# Revit family: 55152_PRESTO_Volta Mitigeur électronique sur plage pour lavabo_FR
name_source: partatom
category: Appareils sanitaires
revit_build: Autodesk Revit 2018 (Build: 20190510_1515(x64)
units: mm (PartAtom-declared; Revit-internal decimal feet)

## family parameters
Basée sur le plan de construction = Non
Cote de connecteur circulaire = Utiliser le diamètre
Couper avec des vides une fois chargée = Non
Partagée = Non
Point de calcul de pièce = Non
Toujours verticalement = Oui
Type d'élément = Normal

## types (1)
- 55152 Presto Volta Mitigeur électronique sur plage pour lavabo
    Adresse = 7, RUE RACINE - 92542 MONTROUGE CEDEX FRANCE
    Charge apparente = 0 VA
    Description = Robinet temporisé mitigeur électronique sur plage pour lavabo
    Diamètre arrivée d'eau = 12 mm  [stored 0.0393701 ft]
    Débit = 8 l/mn par limiteur de débit intégré
    Fabricant = LES ROBINETSPRESTO S.A.
    Facteur de puissance = 1
    Famille produit = Lavabo
    Flux arrivée d'eau = 0.0 L/s
    Garantie = 10
    Groupe produit = -
    Hauteur = 157 mm  [stored 0.515092 ft]
    Longueur = 71 mm
    Matériau = PRESTO - Métal
    Matériau principal = Corps et capot en métal moulé injecté
    Matériau secondaire = -
    Modèle = 55152 Presto Volta Mitigeur électronique sur plage pour lavabo
    Pays fabricant = France
    Perte de charge arrivée d'eau = 0.0 Pa
    Poids = 0.00 kg
    Position hauteur transfo = 0 mm  [stored 0 ft]
    Position longueur transfo = 0 mm  [stored 0 ft]
    Position profondeur transfo = 0 mm  [stored 0 ft]
    Profondeur = 166 mm
    Raccordement = G 3/8"
    SKU produit = 55152
    Tension = 230 V
    URL = http://www.prestodatashare.com
    Variantes = 55152
    Visibilité boîtier électrique = Oui

note: [stored X ft] marks values corroborated as IEEE doubles in the binary element streams (Revit-internal decimal feet)

## geometry (parser evidence)
native form markers: Sweep x1
no freeform markers — native parametric forms only
